# Revit family: Haworth_Janus_SEE_OccasionalTable_Closed
name_source: partatom
category: Furniture
revit_build: Autodesk Revit 2018 (Build: 20170223_1515(x64)
units: mm (PartAtom-declared; Revit-internal decimal feet)

## family parameters
Always vertical = Yes
Cut with Voids When Loaded = No
OmniClass Number = 23.40.70.14.64.21
OmniClass Title = Systems Furniture
Room Calculation Point = No
Shared = No
Work Plane-Based = No

## types (4) — shared parameters
Assembly Code = E2020200
Glide Finish = Haworth _ Polymer _ Black
Manufacturer = Haworth
Revision Number = 2
Size = Verify Final Dim. w/ Haworth
URL = http://www.haworth.com
URL - Product = https://www.haworth.com
Warranty = https://www.haworth.com

## per-type parameters (varying)
| type | Actual Depth | Actual Height | Actual Width | Description | Large | Medium | Small | Wide |
| HCJC-SE-TFCR26-J | 30 1/4" | 13 1/2" | 26" | Haworth Janus SEE! Medium Occasional Table Closed | No | Yes | No | No |
| HCJC-SE-TFCR36-J | 30 1/4" | 13 1/2" | 36 1/4" | Haworth Janus SEE! Wide Occasional Table Closed | No | No | No | Yes |
| HCJC-SE-TFCR54-J | 30 1/4" | 13 1/2" | 54 1/4" | Haworth Janus SEE! Extra Wide Occasional Table Closed | Yes | No | No | No |
| HCJC-SE-TOCQ19-J | 19" | 16 1/2" | 19" | Haworth Janus SEE! Small Occasional Table Closed | No | No | Yes | No |

note: column(s) folded — value = type name in every type: Model

## geometry (parser evidence)
native form markers: Sweep x2
no freeform markers — native parametric forms only
